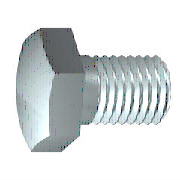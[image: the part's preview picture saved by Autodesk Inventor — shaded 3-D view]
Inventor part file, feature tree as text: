
AUTODESK INVENTOR PART (.ipt)
format: ipt  version: 2025.2 (Build 292293000, 293)  size: 196,096 bytes
history: native  units: mm (DEFAULTED — no unit token found)
features: chamfer x2, other x1, extrude x1, fillet x1, plane x1
ambient origin geometry x7: Origin, YZ Plane, XZ Plane, X Axis, Y Axis, Z Axis, Center Point
bodies: Solid1 (feature_tree)
feature tree (6):
  other  "Körper"
  extrude  "Kopf"  Depth=12.0mm
  chamfer  "Fase1"  Angle=90.0deg  [1 undecoded]
  chamfer  "Fase2"  Distance=8.0mm
  fillet  "Fillet2"  [1 undecoded]
  plane  "Work Plane1"
note: 2 required parameter values undecoded (feature->parameter linkage not recoverable at this tier; creation-order binding heuristic only, values carry confidence <= 0.55)
